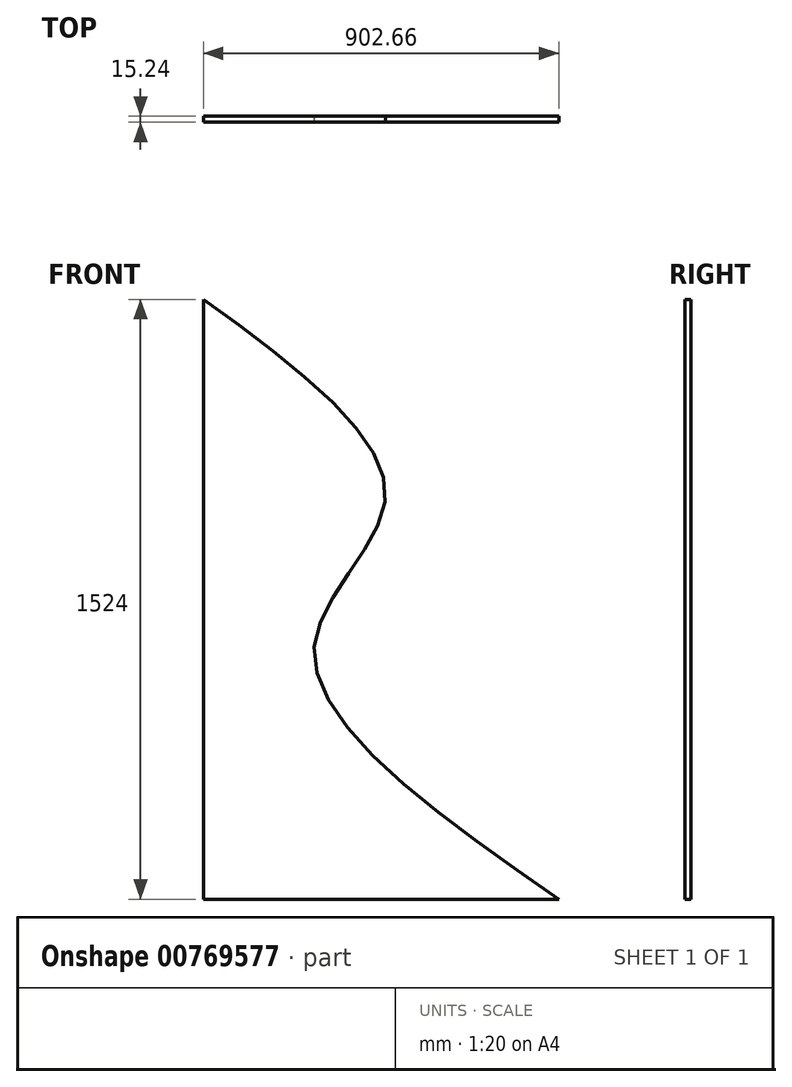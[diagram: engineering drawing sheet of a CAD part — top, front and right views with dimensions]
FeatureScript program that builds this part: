
annotation { "Feature Type Name" : "Feature", "Feature Type Description" : "" }
export const myFeature = defineFeature(function(context is Context, id is Id, definition is map)
    precondition{}
    {
        {
            var Q0;
            Q0=qCreatedBy(makeId("Front.planeOp"),FACE);
            var sketch = newSketch(context, id + "F0", { "sketchPlane" : qUnion([Q0])});
            skLineSegment(sketch, "E0", {"start": v(0, 782.83) * mm, "end": v(0, -741.17) * mm});
            skFitSpline(sketch, "E1", {"points": [v(0, 782.83) * mm, v(461.71, 275.99) * mm, v(281.2, -102.41) * mm, v(902.66, -741.17) * mm], "startDerivative": vector(2076.4, -1510.43) * mm, "endDerivative": vector(2437.78, -1682.04) * mm});
            skLineSegment(sketch, "E2", {"start": v(902.66, -741.17) * mm, "end": v(0, -741.17) * mm});
            skSolve(sketch);
        }
        {
            var Q0;
            Q0 = qSketchRegion(id + "F0", true);
            extrude(context, id + "F1", {"entities" : qUnion([Q0]), "depth" : 15.24 * mm, "offsetDistance" : 30.48 * mm});
        }
    });
